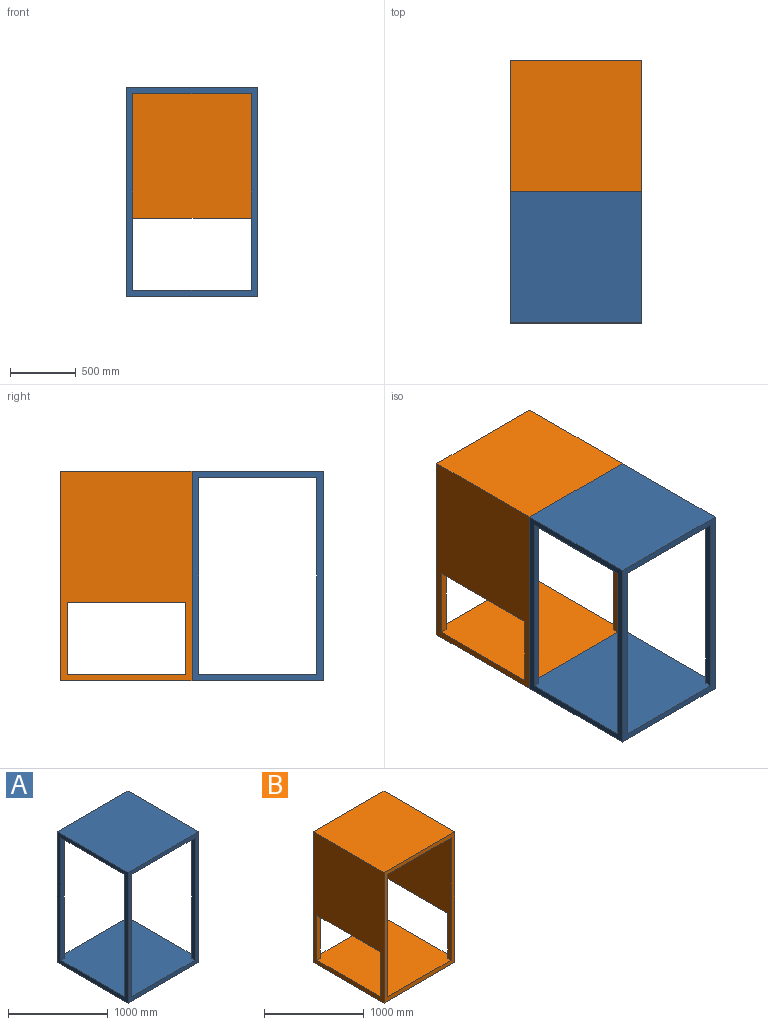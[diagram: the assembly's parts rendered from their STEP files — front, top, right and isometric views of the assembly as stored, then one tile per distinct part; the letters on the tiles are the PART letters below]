
ASSEMBLY  parts=2 mates=1
PART A: 16 faces, bbox 1000x1000x1600 mm
  f0: plane 1600x1000mm, normal (1,0,0), area 250000mm2, adj f4,f5,f6,f7,f8,f11,f14,f15
  f1: plane 1600x1000mm, normal (-1,0,0), area 250000mm2, adj f4,f5,f6,f7,f8,f11,f12,f13
  f2: plane 1500x50mm, normal (-1,0,0), area 75000mm2, adj f6,f8,f11,f14
  f3: plane 1500x50mm, normal (1,0,0), area 75000mm2, adj f6,f8,f11,f13
  f4: plane 1000x1000mm, normal (0,0,1), area 1000000mm2, adj f0,f1,f6,f7
  f5: plane 1000x1000mm, normal (0,0,-1), area 1000000mm2, adj f0,f1,f6,f7
  f6: plane 1600x1000mm, normal (0,1,0), area 250000mm2, adj f0,f1,f2,f3,f4,f5,f8,f11
  f7: plane 1600x1000mm, normal (0,-1,0), area 250000mm2, adj f0,f1,f4,f5,f8,f9,f10,f11
  f8: plane 1000x1000mm, normal (0,0,-1), area 990000mm2, adj f0,f1,f2,f3,f6,f7,f9,f10
  f9: plane 1500x50mm, normal (-1,0,0), area 75000mm2, adj f7,f8,f11,f15
  f10: plane 1500x50mm, normal (1,0,0), area 75000mm2, adj f7,f8,f11,f12
  f11: plane 1000x1000mm, normal (0,0,1), area 990000mm2, adj f0,f1,f2,f3,f6,f7,f9,f10
  f12: plane 1500x50mm, normal (0,1,0), area 75000mm2, adj f1,f8,f10,f11
  f13: plane 1500x50mm, normal (0,-1,0), area 75000mm2, adj f1,f3,f8,f11
  f14: plane 1500x50mm, normal (0,-1,0), area 75000mm2, adj f0,f2,f8,f11
  f15: plane 1500x50mm, normal (0,1,0), area 75000mm2, adj f0,f8,f9,f11
PART B: 20 faces, bbox 1000x1000x1600 mm
  f0: plane 1500x950mm, normal (-1,0,0), area 930000mm2, adj f2,f8,f11,f16,f17,f19
  f1: plane 1500x950mm, normal (1,0,0), area 930000mm2, adj f2,f8,f11,f12,f13,f19
  f2: plane 950x900mm, normal (0,0,-1), area 855000mm2, adj f0,f1,f8,f19
  f3: plane 1600x1000mm, normal (1,0,0), area 1105000mm2, adj f7,f8,f9,f10,f11,f15,f16,f17
  f4: plane 1600x1000mm, normal (-1,0,0), area 1105000mm2, adj f7,f8,f9,f10,f11,f12,f13,f14
  f5: plane 550x50mm, normal (-1,0,0), area 27500mm2, adj f7,f11,f15,f18
  f6: plane 550x50mm, normal (1,0,0), area 27500mm2, adj f7,f11,f14,f18
  f7: plane 1600x1000mm, normal (0,1,0), area 1105000mm2, adj f3,f4,f5,f6,f9,f10,f11,f18
  f8: plane 1600x1000mm, normal (0,-1,0), area 250000mm2, adj f0,f1,f2,f3,f4,f9,f10,f11
  f9: plane 1000x1000mm, normal (0,0,1), area 1000000mm2, adj f3,f4,f7,f8
  f10: plane 1000x1000mm, normal (0,0,-1), area 1000000mm2, adj f3,f4,f7,f8
  f11: plane 1000x1000mm, normal (0,0,1), area 990000mm2, adj f0,f1,f3,f4,f5,f6,f7,f8
  f12: plane 550x50mm, normal (0,1,0), area 27500mm2, adj f1,f4,f11,f13
  f13: plane 900x50mm, normal (0,0,-1), area 45000mm2, adj f1,f4,f12,f14
  f14: plane 550x50mm, normal (0,-1,0), area 27500mm2, adj f4,f6,f11,f13
  f15: plane 550x50mm, normal (0,-1,0), area 27500mm2, adj f3,f5,f11,f16
  f16: plane 900x50mm, normal (0,0,-1), area 45000mm2, adj f0,f3,f15,f17
  f17: plane 550x50mm, normal (0,1,0), area 27500mm2, adj f0,f3,f11,f16
  f18: plane 900x50mm, normal (0,0,-1), area 45000mm2, adj f5,f6,f7,f19
  f19: plane 950x900mm, normal (0,-1,0), area 855000mm2, adj f0,f1,f2,f18
PLACE A t=(-1114.05,-860.49,702.28)mm
PLACE B t=(-1114.05,139.51,702.28)mm
MATE parallel B.f8 <-> A.f6  axis (0,-1,0) through (-1114.05,139.51,702.28)mm
